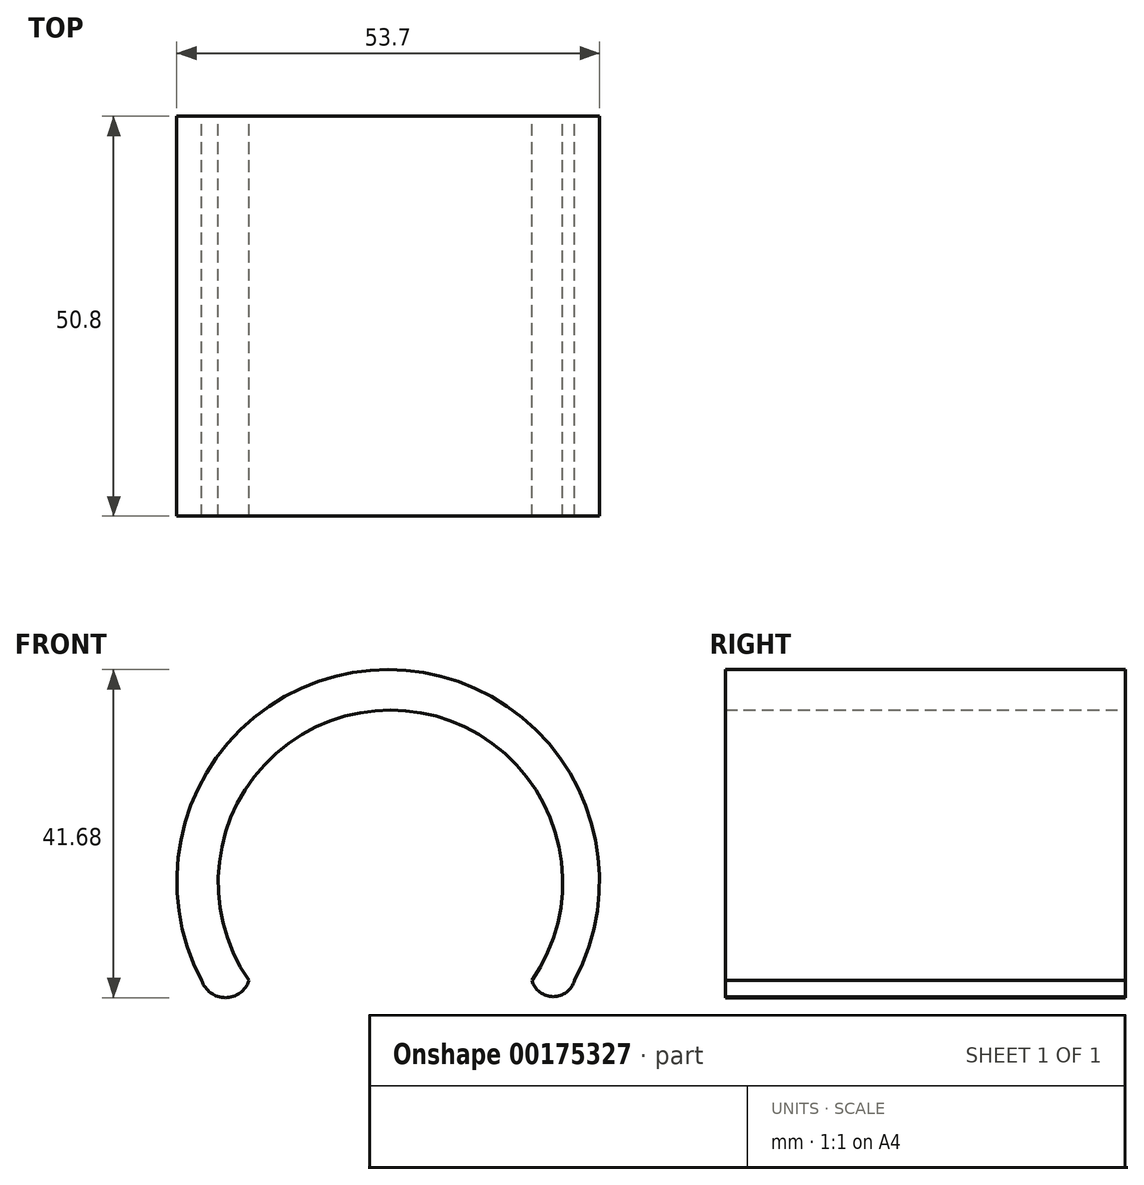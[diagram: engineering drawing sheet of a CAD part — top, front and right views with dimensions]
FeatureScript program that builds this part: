
annotation { "Feature Type Name" : "Feature", "Feature Type Description" : "" }
export const myFeature = defineFeature(function(context is Context, id is Id, definition is map)
    precondition{}
    {
        {
            var Q0;
            Q0=qCreatedBy(makeId("Front.planeOp"),FACE);
            var sketch = newSketch(context, id + "F0", { "sketchPlane" : qUnion([Q0])});
            skArc(sketch, "E0", {"start": v(23.67, 0) * mm, "mid": v(0, 39.5) * mm, "end": v(-23.67, 0) * mm});
            skArc(sketch, "E1", {"start": v(18.26, 0) * mm, "mid": v(0.29, 34.37) * mm, "end": v(-17.68, 0) * mm});
            skArc(sketch, "E2", {"start": v(-23.67, 0) * mm, "mid": v(-20.68, -2.17) * mm, "end": v(-17.68, 0) * mm});
            skArc(sketch, "E3", {"start": v(18.26, 0) * mm, "mid": v(20.97, -2.05) * mm, "end": v(23.67, 0) * mm});
            skSolve(sketch);
        }
        {
            var Q0;
            Q0=makeQuery(id+"F0.imprint","IMPRINT",FACE,{"disambiguationData":[TD([[makeQuery(id+"F0.imprint","IMPRINT",EDGE,{"derivedFrom":sQuery(id+"F0.wireOp",EDGE,"E0")}),1.0]])]});
            extrude(context, id + "F1", {"entities" : qUnion([Q0]), "depth" : 50.8 * mm});
        }
        {
            var Q0;
            Q0=sQuery(id+"F0.wireOp",EDGE,"E1");
            extrude(context, id + "F2", {"bodyType" : ToolBodyType.SURFACE, "surfaceEntities" : qUnion([Q0]), "depth" : 25.4 * mm});
        }
    });
